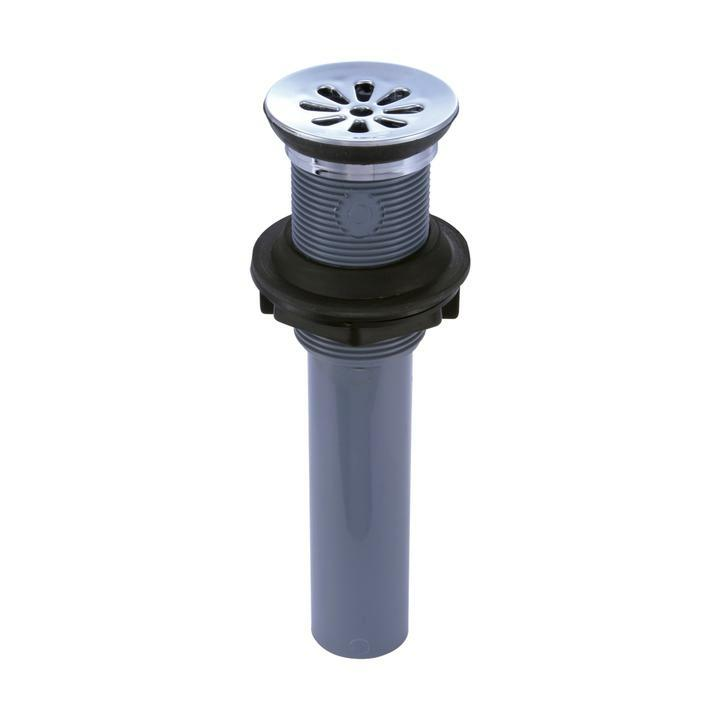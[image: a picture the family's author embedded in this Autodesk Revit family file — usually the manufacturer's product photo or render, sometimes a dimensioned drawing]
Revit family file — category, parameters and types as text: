
# Revit family: 01-1937-11-DESAGÜE SENCILLO PLÁSTICO SIN REBOSE
name_source: partatom
category: Aparatos sanitarios
units: mm (PartAtom-declared; Revit-internal decimal feet)

## family parameters
Activar corte en vistas = No
Anfitrión = Cara
Compartido = No
Corte con vacíos al cargar = No
Cota de conector redondo = Usar diámetro
Mantener orientación de anotación = No
Número OmniClass = 23.31.11.00
Punto de cálculo de habitación = No
Tipo de pieza = Normal

## types (1)
- 01-1937-11
    Acople = 31.8 mm  [stored 0.104331 ft]
    Alto = 185 mm  [stored 0.606955 ft]
    Caucho = Caucho
    Caucho espumoso blanco = Caucho Espumoso blanco
    Conexiones = Tubo para acople en tubería de 1¼”
    Conexión AC = Sí
    Conexión AF = Sí
    Conexión de residuos = No
    Conexión de ventilación = No
    Consumo aproximado a 25 psi = 27
    Descripción = Desague
    Diametro = 57.2 mm
    Diametro Externo = 1 1/4"
    Elevación por defecto = 0 mm  [stored 0 ft]
    Fabricante = Gricol
    Garantia Especifica = 20 Años
    Goteo de Sello = 63 ml/min
    Imagen de tipo = FOTO-DESAGÜE SENCILLO PLÁSTICO SIN REBOSE.jpg
    Link Ficha Tecnica = https://infotecnica.gricol.com
    Materiales del producto = ABS, Polipropileno, Caucho
    Modelo = 01-1937-11
    Plastico - polipropileno + colorante gris = Plastico - polipropileno + colorante gris
    Plastico - polipropileno + colorante negro = Plastico - polipropileno + colorante Negro
    Plastico ABS Cromado = Plastico - ABS Cromado
    Product Name = Desagüe Sencillo Sin Rebose
    Referente Normativo = NTC 5302, ASME A112.18.2 / CSA B125.2
    Resistencia a Corrosión = NTC 1156, Sal Neutral
    Sitio web = https://www.gricol.com
    Temperaturas de trabajo = de 19C° A 62C°
    Tipo de Uso = Domestico
    Torque de Conexioón = 20 Nm
    URL = https://www.gricol.com
    Vida Util = 100000 Ciclos

note: [stored X ft] marks values corroborated as IEEE doubles in the binary element streams (Revit-internal decimal feet)

## geometry (parser evidence)
native form markers: Blend x6, Sweep x4
no freeform markers — native parametric forms only
